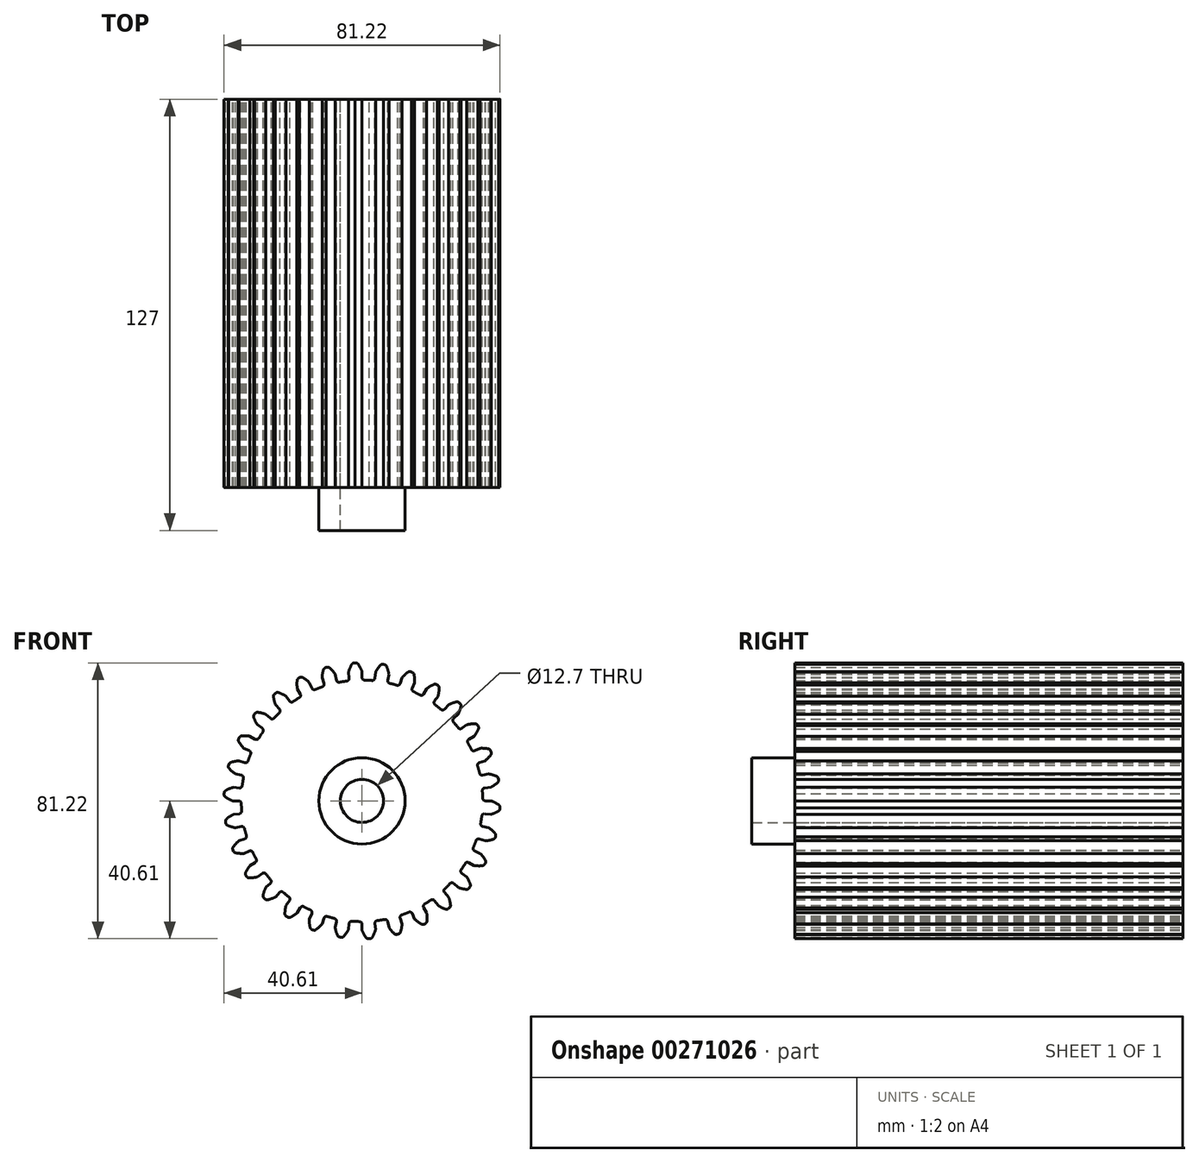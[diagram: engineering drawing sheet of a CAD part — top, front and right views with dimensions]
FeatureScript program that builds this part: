
annotation { "Feature Type Name" : "Feature", "Feature Type Description" : "" }
export const myFeature = defineFeature(function(context is Context, id is Id, definition is map)
    precondition{}
    {
        {
            var Q0;
            Q0=qCreatedBy(makeId("Front.planeOp"),FACE);
            var sketch = newSketch(context, id + "F0", { "sketchPlane" : qUnion([Q0])});
            skArc(sketch, "E0", {"start": v(-4.48, 35.28) * mm, "mid": v(1.86, -35.51) * mm, "end": v(0.77, 35.55) * mm});
            skLineSegment(sketch, "E1", {"start": v(0, 0) * mm, "end": v(-3.21, 61.32) * mm, "construction": true});
            skLineSegment(sketch, "E2", {"start": v(-1.83, 40.61) * mm, "end": v(-2.13, 40.61) * mm});
            skLineSegment(sketch, "E3", {"start": v(0, 38.1) * mm, "end": v(0, 36.34) * mm});
            skArc(sketch, "E4.trimOffspring", {"start": v(0, 38.1) * mm, "mid": v(-0.52, 39.23) * mm, "end": v(-1.2, 40.3) * mm});
            skLineSegment(sketch, "E5.MirrorCS", {"start": v(-2.43, 40.58) * mm, "end": v(-2.13, 40.61) * mm});
            skArc(sketch, "E6.MirrorCS", {"start": v(-3.98, 37.9) * mm, "mid": v(-3.58, 39.07) * mm, "end": v(-3.03, 40.2) * mm});
            skLineSegment(sketch, "E7.MirrorCS", {"start": v(-3.98, 37.9) * mm, "end": v(-3.8, 36.14) * mm});
            skPoint(sketch, "E8.orphan", {"position": v(-3.59, 34.15) * mm});
            skPoint(sketch, "E9.orphan", {"position": v(0, 34.34) * mm});
            skPoint(sketch, "E10.visualSharp", {"position": v(-2.81, 40.54) * mm});
            skArc(sketch, "E10.filletArc", {"start": v(-2.43, 40.58) * mm, "mid": v(-2.77, 40.46) * mm, "end": v(-3.03, 40.2) * mm});
            skPoint(sketch, "E11.visualSharp", {"position": v(-1.44, 40.61) * mm});
            skArc(sketch, "E11.filletArc", {"start": v(-1.2, 40.3) * mm, "mid": v(-1.47, 40.53) * mm, "end": v(-1.83, 40.61) * mm});
            skPoint(sketch, "E12.visualSharp", {"position": v(0, 35.56) * mm});
            skArc(sketch, "E12.filletArc", {"start": v(0, 36.34) * mm, "mid": v(0.22, 35.79) * mm, "end": v(0.77, 35.55) * mm});
            skPoint(sketch, "E13.visualSharp", {"position": v(-3.72, 35.37) * mm});
            skArc(sketch, "E13.filletArc", {"start": v(-4.48, 35.28) * mm, "mid": v(-3.96, 35.57) * mm, "end": v(-3.8, 36.14) * mm});
            skArc(sketch, "E14.1.0", {"start": v(-11.72, 33.57) * mm, "mid": v(-11.27, 33.97) * mm, "end": v(-11.23, 34.56) * mm});
            skLineSegment(sketch, "E14.1.1", {"start": v(-11.77, 36.24) * mm, "end": v(-11.23, 34.56) * mm});
            skArc(sketch, "E14.1.2", {"start": v(-11.77, 36.24) * mm, "mid": v(-11.63, 37.48) * mm, "end": v(-11.32, 38.69) * mm});
            skArc(sketch, "E14.1.3", {"start": v(-10.81, 39.2) * mm, "mid": v(-11.12, 39) * mm, "end": v(-11.32, 38.69) * mm});
            skLineSegment(sketch, "E14.1.4", {"start": v(-10.81, 39.2) * mm, "end": v(-10.53, 39.28) * mm});
            skLineSegment(sketch, "E14.1.5", {"start": v(-10.23, 39.35) * mm, "end": v(-10.53, 39.28) * mm});
            skArc(sketch, "E14.1.6", {"start": v(-9.54, 39.16) * mm, "mid": v(-9.87, 39.34) * mm, "end": v(-10.23, 39.35) * mm});
            skArc(sketch, "E14.1.7", {"start": v(-7.92, 37.27) * mm, "mid": v(-8.67, 38.27) * mm, "end": v(-9.54, 39.16) * mm});
            skLineSegment(sketch, "E14.1.8", {"start": v(-7.92, 37.27) * mm, "end": v(-7.56, 35.54) * mm});
            skArc(sketch, "E14.1.9", {"start": v(-7.56, 35.54) * mm, "mid": v(-7.22, 35.05) * mm, "end": v(-6.64, 34.93) * mm});
            skArc(sketch, "E14.2.0", {"start": v(-18.44, 30.4) * mm, "mid": v(-18.09, 30.88) * mm, "end": v(-18.17, 31.47) * mm});
            skLineSegment(sketch, "E14.2.1", {"start": v(-19.05, 33) * mm, "end": v(-18.17, 31.47) * mm});
            skArc(sketch, "E14.2.2", {"start": v(-19.05, 33) * mm, "mid": v(-19.16, 34.24) * mm, "end": v(-19.11, 35.49) * mm});
            skArc(sketch, "E14.2.3", {"start": v(-18.72, 36.09) * mm, "mid": v(-18.99, 35.84) * mm, "end": v(-19.11, 35.49) * mm});
            skLineSegment(sketch, "E14.2.4", {"start": v(-18.72, 36.09) * mm, "end": v(-18.46, 36.24) * mm});
            skLineSegment(sketch, "E14.2.5", {"start": v(-18.2, 36.36) * mm, "end": v(-18.46, 36.24) * mm});
            skArc(sketch, "E14.2.6", {"start": v(-17.48, 36.32) * mm, "mid": v(-17.83, 36.43) * mm, "end": v(-18.2, 36.36) * mm});
            skArc(sketch, "E14.2.7", {"start": v(-15.5, 34.8) * mm, "mid": v(-16.44, 35.63) * mm, "end": v(-17.48, 36.32) * mm});
            skLineSegment(sketch, "E14.2.8", {"start": v(-15.5, 34.8) * mm, "end": v(-14.78, 33.2) * mm});
            skArc(sketch, "E14.2.9", {"start": v(-14.78, 33.2) * mm, "mid": v(-14.35, 32.79) * mm, "end": v(-13.76, 32.8) * mm});
            skArc(sketch, "E14.3.0", {"start": v(-24.36, 25.9) * mm, "mid": v(-24.11, 26.45) * mm, "end": v(-24.32, 27) * mm});
            skLineSegment(sketch, "E14.3.1", {"start": v(-25.5, 28.31) * mm, "end": v(-24.32, 27) * mm});
            skArc(sketch, "E14.3.2", {"start": v(-25.5, 28.31) * mm, "mid": v(-25.86, 29.5) * mm, "end": v(-26.07, 30.74) * mm});
            skArc(sketch, "E14.3.3", {"start": v(-25.82, 31.4) * mm, "mid": v(-26.03, 31.1) * mm, "end": v(-26.07, 30.74) * mm});
            skLineSegment(sketch, "E14.3.4", {"start": v(-25.82, 31.4) * mm, "end": v(-25.6, 31.6) * mm});
            skLineSegment(sketch, "E14.3.5", {"start": v(-25.35, 31.78) * mm, "end": v(-25.6, 31.6) * mm});
            skArc(sketch, "E14.3.6", {"start": v(-24.65, 31.9) * mm, "mid": v(-25.01, 31.92) * mm, "end": v(-25.35, 31.78) * mm});
            skArc(sketch, "E14.3.7", {"start": v(-22.4, 30.82) * mm, "mid": v(-23.49, 31.43) * mm, "end": v(-24.65, 31.9) * mm});
            skLineSegment(sketch, "E14.3.8", {"start": v(-22.4, 30.82) * mm, "end": v(-21.36, 29.4) * mm});
            skArc(sketch, "E14.3.9", {"start": v(-21.36, 29.4) * mm, "mid": v(-20.85, 29.09) * mm, "end": v(-20.27, 29.21) * mm});
            skArc(sketch, "E14.4.0", {"start": v(-29.21, 20.27) * mm, "mid": v(-29.09, 20.85) * mm, "end": v(-29.4, 21.36) * mm});
            skLineSegment(sketch, "E14.4.1", {"start": v(-30.82, 22.4) * mm, "end": v(-29.4, 21.36) * mm});
            skArc(sketch, "E14.4.2", {"start": v(-30.82, 22.4) * mm, "mid": v(-31.43, 23.49) * mm, "end": v(-31.9, 24.65) * mm});
            skArc(sketch, "E14.4.3", {"start": v(-31.78, 25.35) * mm, "mid": v(-31.92, 25.01) * mm, "end": v(-31.9, 24.65) * mm});
            skLineSegment(sketch, "E14.4.4", {"start": v(-31.78, 25.35) * mm, "end": v(-31.6, 25.6) * mm});
            skLineSegment(sketch, "E14.4.5", {"start": v(-31.4, 25.82) * mm, "end": v(-31.6, 25.6) * mm});
            skArc(sketch, "E14.4.6", {"start": v(-30.74, 26.07) * mm, "mid": v(-31.1, 26.03) * mm, "end": v(-31.4, 25.82) * mm});
            skArc(sketch, "E14.4.7", {"start": v(-28.31, 25.5) * mm, "mid": v(-29.5, 25.86) * mm, "end": v(-30.74, 26.07) * mm});
            skLineSegment(sketch, "E14.4.8", {"start": v(-28.31, 25.5) * mm, "end": v(-27, 24.32) * mm});
            skArc(sketch, "E14.4.9", {"start": v(-27, 24.32) * mm, "mid": v(-26.45, 24.11) * mm, "end": v(-25.9, 24.36) * mm});
            skArc(sketch, "E14.5.0", {"start": v(-32.8, 13.76) * mm, "mid": v(-32.79, 14.35) * mm, "end": v(-33.2, 14.78) * mm});
            skLineSegment(sketch, "E14.5.1", {"start": v(-34.8, 15.5) * mm, "end": v(-33.2, 14.78) * mm});
            skArc(sketch, "E14.5.2", {"start": v(-34.8, 15.5) * mm, "mid": v(-35.63, 16.44) * mm, "end": v(-36.32, 17.48) * mm});
            skArc(sketch, "E14.5.3", {"start": v(-36.36, 18.2) * mm, "mid": v(-36.43, 17.83) * mm, "end": v(-36.32, 17.48) * mm});
            skLineSegment(sketch, "E14.5.4", {"start": v(-36.36, 18.2) * mm, "end": v(-36.24, 18.46) * mm});
            skLineSegment(sketch, "E14.5.5", {"start": v(-36.09, 18.72) * mm, "end": v(-36.24, 18.46) * mm});
            skArc(sketch, "E14.5.6", {"start": v(-35.49, 19.11) * mm, "mid": v(-35.84, 18.99) * mm, "end": v(-36.09, 18.72) * mm});
            skArc(sketch, "E14.5.7", {"start": v(-33, 19.05) * mm, "mid": v(-34.24, 19.16) * mm, "end": v(-35.49, 19.11) * mm});
            skLineSegment(sketch, "E14.5.8", {"start": v(-33, 19.05) * mm, "end": v(-31.47, 18.17) * mm});
            skArc(sketch, "E14.5.9", {"start": v(-31.47, 18.17) * mm, "mid": v(-30.88, 18.09) * mm, "end": v(-30.4, 18.44) * mm});
            skArc(sketch, "E14.6.0", {"start": v(-34.93, 6.64) * mm, "mid": v(-35.05, 7.22) * mm, "end": v(-35.54, 7.56) * mm});
            skLineSegment(sketch, "E14.6.1", {"start": v(-37.27, 7.92) * mm, "end": v(-35.54, 7.56) * mm});
            skArc(sketch, "E14.6.2", {"start": v(-37.27, 7.92) * mm, "mid": v(-38.27, 8.67) * mm, "end": v(-39.16, 9.54) * mm});
            skArc(sketch, "E14.6.3", {"start": v(-39.35, 10.23) * mm, "mid": v(-39.34, 9.87) * mm, "end": v(-39.16, 9.54) * mm});
            skLineSegment(sketch, "E14.6.4", {"start": v(-39.35, 10.23) * mm, "end": v(-39.28, 10.53) * mm});
            skLineSegment(sketch, "E14.6.5", {"start": v(-39.2, 10.81) * mm, "end": v(-39.28, 10.53) * mm});
            skArc(sketch, "E14.6.6", {"start": v(-38.69, 11.32) * mm, "mid": v(-39, 11.12) * mm, "end": v(-39.2, 10.81) * mm});
            skArc(sketch, "E14.6.7", {"start": v(-36.24, 11.77) * mm, "mid": v(-37.48, 11.63) * mm, "end": v(-38.69, 11.32) * mm});
            skLineSegment(sketch, "E14.6.8", {"start": v(-36.24, 11.77) * mm, "end": v(-34.56, 11.23) * mm});
            skArc(sketch, "E14.6.9", {"start": v(-34.56, 11.23) * mm, "mid": v(-33.97, 11.27) * mm, "end": v(-33.57, 11.72) * mm});
            skArc(sketch, "E14.7.0", {"start": v(-35.55, -0.77) * mm, "mid": v(-35.79, -0.22) * mm, "end": v(-36.34, 0) * mm});
            skLineSegment(sketch, "E14.7.1", {"start": v(-38.1, 0) * mm, "end": v(-36.34, 0) * mm});
            skArc(sketch, "E14.7.2", {"start": v(-38.1, 0) * mm, "mid": v(-39.23, 0.52) * mm, "end": v(-40.3, 1.2) * mm});
            skArc(sketch, "E14.7.3", {"start": v(-40.61, 1.83) * mm, "mid": v(-40.53, 1.47) * mm, "end": v(-40.3, 1.2) * mm});
            skLineSegment(sketch, "E14.7.4", {"start": v(-40.61, 1.83) * mm, "end": v(-40.61, 2.13) * mm});
            skLineSegment(sketch, "E14.7.5", {"start": v(-40.58, 2.43) * mm, "end": v(-40.61, 2.13) * mm});
            skArc(sketch, "E14.7.6", {"start": v(-40.2, 3.03) * mm, "mid": v(-40.46, 2.77) * mm, "end": v(-40.58, 2.43) * mm});
            skArc(sketch, "E14.7.7", {"start": v(-37.9, 3.98) * mm, "mid": v(-39.07, 3.58) * mm, "end": v(-40.2, 3.03) * mm});
            skLineSegment(sketch, "E14.7.8", {"start": v(-37.9, 3.98) * mm, "end": v(-36.14, 3.8) * mm});
            skArc(sketch, "E14.7.9", {"start": v(-36.14, 3.8) * mm, "mid": v(-35.57, 3.96) * mm, "end": v(-35.28, 4.48) * mm});
            skArc(sketch, "E14.8.0", {"start": v(-34.61, -8.15) * mm, "mid": v(-34.96, -7.66) * mm, "end": v(-35.54, -7.56) * mm});
            skLineSegment(sketch, "E14.8.1", {"start": v(-37.27, -7.92) * mm, "end": v(-35.54, -7.56) * mm});
            skArc(sketch, "E14.8.2", {"start": v(-37.27, -7.92) * mm, "mid": v(-38.49, -7.64) * mm, "end": v(-39.66, -7.21) * mm});
            skArc(sketch, "E14.8.3", {"start": v(-40.1, -6.66) * mm, "mid": v(-39.95, -6.99) * mm, "end": v(-39.66, -7.21) * mm});
            skLineSegment(sketch, "E14.8.4", {"start": v(-40.1, -6.66) * mm, "end": v(-40.17, -6.36) * mm});
            skLineSegment(sketch, "E14.8.5", {"start": v(-40.2, -6.06) * mm, "end": v(-40.17, -6.36) * mm});
            skArc(sketch, "E14.8.6", {"start": v(-39.95, -5.4) * mm, "mid": v(-40.15, -5.7) * mm, "end": v(-40.2, -6.06) * mm});
            skArc(sketch, "E14.8.7", {"start": v(-37.9, -3.98) * mm, "mid": v(-38.96, -4.62) * mm, "end": v(-39.95, -5.4) * mm});
            skLineSegment(sketch, "E14.8.8", {"start": v(-37.9, -3.98) * mm, "end": v(-36.14, -3.8) * mm});
            skArc(sketch, "E14.8.9", {"start": v(-36.14, -3.8) * mm, "mid": v(-35.62, -3.52) * mm, "end": v(-35.44, -2.95) * mm});
            skArc(sketch, "E14.9.0", {"start": v(-32.16, -15.16) * mm, "mid": v(-32.6, -14.76) * mm, "end": v(-33.2, -14.78) * mm});
            skLineSegment(sketch, "E14.9.1", {"start": v(-34.8, -15.5) * mm, "end": v(-33.2, -14.78) * mm});
            skArc(sketch, "E14.9.2", {"start": v(-34.8, -15.5) * mm, "mid": v(-36.06, -15.48) * mm, "end": v(-37.3, -15.3) * mm});
            skArc(sketch, "E14.9.3", {"start": v(-37.85, -14.85) * mm, "mid": v(-37.62, -15.14) * mm, "end": v(-37.3, -15.3) * mm});
            skLineSegment(sketch, "E14.9.4", {"start": v(-37.85, -14.85) * mm, "end": v(-37.97, -14.57) * mm});
            skLineSegment(sketch, "E14.9.5", {"start": v(-38.06, -14.29) * mm, "end": v(-37.97, -14.57) * mm});
            skArc(sketch, "E14.9.6", {"start": v(-37.95, -13.58) * mm, "mid": v(-38.1, -13.92) * mm, "end": v(-38.06, -14.29) * mm});
            skArc(sketch, "E14.9.7", {"start": v(-36.24, -11.77) * mm, "mid": v(-37.15, -12.62) * mm, "end": v(-37.95, -13.58) * mm});
            skLineSegment(sketch, "E14.9.8", {"start": v(-36.24, -11.77) * mm, "end": v(-34.56, -11.23) * mm});
            skArc(sketch, "E14.9.9", {"start": v(-34.56, -11.23) * mm, "mid": v(-34.1, -10.85) * mm, "end": v(-34.05, -10.25) * mm});
            skArc(sketch, "E14.10.0", {"start": v(-28.3, -21.52) * mm, "mid": v(-28.82, -21.22) * mm, "end": v(-29.4, -21.36) * mm});
            skLineSegment(sketch, "E14.10.1", {"start": v(-30.82, -22.4) * mm, "end": v(-29.4, -21.36) * mm});
            skArc(sketch, "E14.10.2", {"start": v(-30.82, -22.4) * mm, "mid": v(-32.05, -22.64) * mm, "end": v(-33.3, -22.72) * mm});
            skArc(sketch, "E14.10.3", {"start": v(-33.93, -22.4) * mm, "mid": v(-33.65, -22.63) * mm, "end": v(-33.3, -22.72) * mm});
            skLineSegment(sketch, "E14.10.4", {"start": v(-33.93, -22.4) * mm, "end": v(-34.1, -22.15) * mm});
            skLineSegment(sketch, "E14.10.5", {"start": v(-34.26, -21.9) * mm, "end": v(-34.1, -22.15) * mm});
            skArc(sketch, "E14.10.6", {"start": v(-34.3, -21.18) * mm, "mid": v(-34.36, -21.54) * mm, "end": v(-34.26, -21.9) * mm});
            skArc(sketch, "E14.10.7", {"start": v(-33, -19.05) * mm, "mid": v(-33.72, -20.07) * mm, "end": v(-34.3, -21.18) * mm});
            skLineSegment(sketch, "E14.10.8", {"start": v(-33, -19.05) * mm, "end": v(-31.47, -18.17) * mm});
            skArc(sketch, "E14.10.9", {"start": v(-31.47, -18.17) * mm, "mid": v(-31.1, -17.7) * mm, "end": v(-31.17, -17.1) * mm});
            skArc(sketch, "E14.11.0", {"start": v(-23.22, -26.94) * mm, "mid": v(-23.78, -26.75) * mm, "end": v(-24.32, -27) * mm});
            skLineSegment(sketch, "E14.11.1", {"start": v(-25.5, -28.31) * mm, "end": v(-24.32, -27) * mm});
            skArc(sketch, "E14.11.2", {"start": v(-25.5, -28.31) * mm, "mid": v(-26.64, -28.8) * mm, "end": v(-27.85, -29.14) * mm});
            skArc(sketch, "E14.11.3", {"start": v(-28.54, -28.96) * mm, "mid": v(-28.21, -29.13) * mm, "end": v(-27.85, -29.14) * mm});
            skLineSegment(sketch, "E14.11.4", {"start": v(-28.54, -28.96) * mm, "end": v(-28.76, -28.76) * mm});
            skLineSegment(sketch, "E14.11.5", {"start": v(-28.96, -28.54) * mm, "end": v(-28.76, -28.76) * mm});
            skArc(sketch, "E14.11.6", {"start": v(-29.14, -27.85) * mm, "mid": v(-29.13, -28.21) * mm, "end": v(-28.96, -28.54) * mm});
            skArc(sketch, "E14.11.7", {"start": v(-28.31, -25.5) * mm, "mid": v(-28.8, -26.64) * mm, "end": v(-29.14, -27.85) * mm});
            skLineSegment(sketch, "E14.11.8", {"start": v(-28.31, -25.5) * mm, "end": v(-27, -24.32) * mm});
            skArc(sketch, "E14.11.9", {"start": v(-27, -24.32) * mm, "mid": v(-26.75, -23.78) * mm, "end": v(-26.94, -23.22) * mm});
            skArc(sketch, "E14.12.0", {"start": v(-17.1, -31.17) * mm, "mid": v(-17.7, -31.1) * mm, "end": v(-18.17, -31.47) * mm});
            skLineSegment(sketch, "E14.12.1", {"start": v(-19.05, -33) * mm, "end": v(-18.17, -31.47) * mm});
            skArc(sketch, "E14.12.2", {"start": v(-19.05, -33) * mm, "mid": v(-20.07, -33.72) * mm, "end": v(-21.18, -34.3) * mm});
            skArc(sketch, "E14.12.3", {"start": v(-21.9, -34.26) * mm, "mid": v(-21.54, -34.36) * mm, "end": v(-21.18, -34.3) * mm});
            skLineSegment(sketch, "E14.12.4", {"start": v(-21.9, -34.26) * mm, "end": v(-22.15, -34.1) * mm});
            skLineSegment(sketch, "E14.12.5", {"start": v(-22.4, -33.93) * mm, "end": v(-22.15, -34.1) * mm});
            skArc(sketch, "E14.12.6", {"start": v(-22.72, -33.3) * mm, "mid": v(-22.63, -33.65) * mm, "end": v(-22.4, -33.93) * mm});
            skArc(sketch, "E14.12.7", {"start": v(-22.4, -30.82) * mm, "mid": v(-22.64, -32.05) * mm, "end": v(-22.72, -33.3) * mm});
            skLineSegment(sketch, "E14.12.8", {"start": v(-22.4, -30.82) * mm, "end": v(-21.36, -29.4) * mm});
            skArc(sketch, "E14.12.9", {"start": v(-21.36, -29.4) * mm, "mid": v(-21.22, -28.82) * mm, "end": v(-21.52, -28.3) * mm});
            skArc(sketch, "E14.13.0", {"start": v(-10.25, -34.05) * mm, "mid": v(-10.85, -34.1) * mm, "end": v(-11.23, -34.56) * mm});
            skLineSegment(sketch, "E14.13.1", {"start": v(-11.77, -36.24) * mm, "end": v(-11.23, -34.56) * mm});
            skArc(sketch, "E14.13.2", {"start": v(-11.77, -36.24) * mm, "mid": v(-12.62, -37.15) * mm, "end": v(-13.58, -37.95) * mm});
            skArc(sketch, "E14.13.3", {"start": v(-14.29, -38.06) * mm, "mid": v(-13.92, -38.1) * mm, "end": v(-13.58, -37.95) * mm});
            skLineSegment(sketch, "E14.13.4", {"start": v(-14.29, -38.06) * mm, "end": v(-14.57, -37.97) * mm});
            skLineSegment(sketch, "E14.13.5", {"start": v(-14.85, -37.85) * mm, "end": v(-14.57, -37.97) * mm});
            skArc(sketch, "E14.13.6", {"start": v(-15.3, -37.3) * mm, "mid": v(-15.14, -37.62) * mm, "end": v(-14.85, -37.85) * mm});
            skArc(sketch, "E14.13.7", {"start": v(-15.5, -34.8) * mm, "mid": v(-15.48, -36.06) * mm, "end": v(-15.3, -37.3) * mm});
            skLineSegment(sketch, "E14.13.8", {"start": v(-15.5, -34.8) * mm, "end": v(-14.78, -33.2) * mm});
            skArc(sketch, "E14.13.9", {"start": v(-14.78, -33.2) * mm, "mid": v(-14.76, -32.6) * mm, "end": v(-15.16, -32.16) * mm});
            skArc(sketch, "E14.14.0", {"start": v(-2.95, -35.44) * mm, "mid": v(-3.52, -35.62) * mm, "end": v(-3.8, -36.14) * mm});
            skLineSegment(sketch, "E14.14.1", {"start": v(-3.98, -37.9) * mm, "end": v(-3.8, -36.14) * mm});
            skArc(sketch, "E14.14.2", {"start": v(-3.98, -37.9) * mm, "mid": v(-4.62, -38.96) * mm, "end": v(-5.4, -39.95) * mm});
            skArc(sketch, "E14.14.3", {"start": v(-6.06, -40.2) * mm, "mid": v(-5.7, -40.15) * mm, "end": v(-5.4, -39.95) * mm});
            skLineSegment(sketch, "E14.14.4", {"start": v(-6.06, -40.2) * mm, "end": v(-6.36, -40.17) * mm});
            skLineSegment(sketch, "E14.14.5", {"start": v(-6.66, -40.1) * mm, "end": v(-6.36, -40.17) * mm});
            skArc(sketch, "E14.14.6", {"start": v(-7.21, -39.66) * mm, "mid": v(-6.99, -39.95) * mm, "end": v(-6.66, -40.1) * mm});
            skArc(sketch, "E14.14.7", {"start": v(-7.92, -37.27) * mm, "mid": v(-7.64, -38.49) * mm, "end": v(-7.21, -39.66) * mm});
            skLineSegment(sketch, "E14.14.8", {"start": v(-7.92, -37.27) * mm, "end": v(-7.56, -35.54) * mm});
            skArc(sketch, "E14.14.9", {"start": v(-7.56, -35.54) * mm, "mid": v(-7.66, -34.96) * mm, "end": v(-8.15, -34.61) * mm});
            skArc(sketch, "E14.15.0", {"start": v(4.48, -35.28) * mm, "mid": v(3.96, -35.57) * mm, "end": v(3.8, -36.14) * mm});
            skLineSegment(sketch, "E14.15.1", {"start": v(3.98, -37.9) * mm, "end": v(3.8, -36.14) * mm});
            skArc(sketch, "E14.15.2", {"start": v(3.98, -37.9) * mm, "mid": v(3.58, -39.07) * mm, "end": v(3.03, -40.2) * mm});
            skArc(sketch, "E14.15.3", {"start": v(2.43, -40.58) * mm, "mid": v(2.77, -40.46) * mm, "end": v(3.03, -40.2) * mm});
            skLineSegment(sketch, "E14.15.4", {"start": v(2.43, -40.58) * mm, "end": v(2.13, -40.61) * mm});
            skLineSegment(sketch, "E14.15.5", {"start": v(1.83, -40.61) * mm, "end": v(2.13, -40.61) * mm});
            skArc(sketch, "E14.15.6", {"start": v(1.2, -40.3) * mm, "mid": v(1.47, -40.53) * mm, "end": v(1.83, -40.61) * mm});
            skArc(sketch, "E14.15.7", {"start": v(0, -38.1) * mm, "mid": v(0.52, -39.23) * mm, "end": v(1.2, -40.3) * mm});
            skLineSegment(sketch, "E14.15.8", {"start": v(0, -38.1) * mm, "end": v(0, -36.34) * mm});
            skArc(sketch, "E14.15.9", {"start": v(0, -36.34) * mm, "mid": v(-0.22, -35.79) * mm, "end": v(-0.77, -35.55) * mm});
            skArc(sketch, "E14.16.0", {"start": v(11.72, -33.57) * mm, "mid": v(11.27, -33.97) * mm, "end": v(11.23, -34.56) * mm});
            skLineSegment(sketch, "E14.16.1", {"start": v(11.77, -36.24) * mm, "end": v(11.23, -34.56) * mm});
            skArc(sketch, "E14.16.2", {"start": v(11.77, -36.24) * mm, "mid": v(11.63, -37.48) * mm, "end": v(11.32, -38.69) * mm});
            skArc(sketch, "E14.16.3", {"start": v(10.81, -39.2) * mm, "mid": v(11.12, -39) * mm, "end": v(11.32, -38.69) * mm});
            skLineSegment(sketch, "E14.16.4", {"start": v(10.81, -39.2) * mm, "end": v(10.53, -39.28) * mm});
            skLineSegment(sketch, "E14.16.5", {"start": v(10.23, -39.35) * mm, "end": v(10.53, -39.28) * mm});
            skArc(sketch, "E14.16.6", {"start": v(9.54, -39.16) * mm, "mid": v(9.87, -39.34) * mm, "end": v(10.23, -39.35) * mm});
            skArc(sketch, "E14.16.7", {"start": v(7.92, -37.27) * mm, "mid": v(8.67, -38.27) * mm, "end": v(9.54, -39.16) * mm});
            skLineSegment(sketch, "E14.16.8", {"start": v(7.92, -37.27) * mm, "end": v(7.56, -35.54) * mm});
            skArc(sketch, "E14.16.9", {"start": v(7.56, -35.54) * mm, "mid": v(7.22, -35.05) * mm, "end": v(6.64, -34.93) * mm});
            skArc(sketch, "E14.17.0", {"start": v(18.44, -30.4) * mm, "mid": v(18.09, -30.88) * mm, "end": v(18.17, -31.47) * mm});
            skLineSegment(sketch, "E14.17.1", {"start": v(19.05, -33) * mm, "end": v(18.17, -31.47) * mm});
            skArc(sketch, "E14.17.2", {"start": v(19.05, -33) * mm, "mid": v(19.16, -34.24) * mm, "end": v(19.11, -35.49) * mm});
            skArc(sketch, "E14.17.3", {"start": v(18.72, -36.09) * mm, "mid": v(18.99, -35.84) * mm, "end": v(19.11, -35.49) * mm});
            skLineSegment(sketch, "E14.17.4", {"start": v(18.72, -36.09) * mm, "end": v(18.46, -36.24) * mm});
            skLineSegment(sketch, "E14.17.5", {"start": v(18.2, -36.36) * mm, "end": v(18.46, -36.24) * mm});
            skArc(sketch, "E14.17.6", {"start": v(17.48, -36.32) * mm, "mid": v(17.83, -36.43) * mm, "end": v(18.2, -36.36) * mm});
            skArc(sketch, "E14.17.7", {"start": v(15.5, -34.8) * mm, "mid": v(16.44, -35.63) * mm, "end": v(17.48, -36.32) * mm});
            skLineSegment(sketch, "E14.17.8", {"start": v(15.5, -34.8) * mm, "end": v(14.78, -33.2) * mm});
            skArc(sketch, "E14.17.9", {"start": v(14.78, -33.2) * mm, "mid": v(14.35, -32.79) * mm, "end": v(13.76, -32.8) * mm});
            skArc(sketch, "E14.18.0", {"start": v(24.36, -25.9) * mm, "mid": v(24.11, -26.45) * mm, "end": v(24.32, -27) * mm});
            skLineSegment(sketch, "E14.18.1", {"start": v(25.5, -28.31) * mm, "end": v(24.32, -27) * mm});
            skArc(sketch, "E14.18.2", {"start": v(25.5, -28.31) * mm, "mid": v(25.86, -29.5) * mm, "end": v(26.07, -30.74) * mm});
            skArc(sketch, "E14.18.3", {"start": v(25.82, -31.4) * mm, "mid": v(26.03, -31.1) * mm, "end": v(26.07, -30.74) * mm});
            skLineSegment(sketch, "E14.18.4", {"start": v(25.82, -31.4) * mm, "end": v(25.6, -31.6) * mm});
            skLineSegment(sketch, "E14.18.5", {"start": v(25.35, -31.78) * mm, "end": v(25.6, -31.6) * mm});
            skArc(sketch, "E14.18.6", {"start": v(24.65, -31.9) * mm, "mid": v(25.01, -31.92) * mm, "end": v(25.35, -31.78) * mm});
            skArc(sketch, "E14.18.7", {"start": v(22.4, -30.82) * mm, "mid": v(23.49, -31.43) * mm, "end": v(24.65, -31.9) * mm});
            skLineSegment(sketch, "E14.18.8", {"start": v(22.4, -30.82) * mm, "end": v(21.36, -29.4) * mm});
            skArc(sketch, "E14.18.9", {"start": v(21.36, -29.4) * mm, "mid": v(20.85, -29.09) * mm, "end": v(20.27, -29.21) * mm});
            skArc(sketch, "E14.19.0", {"start": v(29.21, -20.27) * mm, "mid": v(29.09, -20.85) * mm, "end": v(29.4, -21.36) * mm});
            skLineSegment(sketch, "E14.19.1", {"start": v(30.82, -22.4) * mm, "end": v(29.4, -21.36) * mm});
            skArc(sketch, "E14.19.2", {"start": v(30.82, -22.4) * mm, "mid": v(31.43, -23.49) * mm, "end": v(31.9, -24.65) * mm});
            skArc(sketch, "E14.19.3", {"start": v(31.78, -25.35) * mm, "mid": v(31.92, -25.01) * mm, "end": v(31.9, -24.65) * mm});
            skLineSegment(sketch, "E14.19.4", {"start": v(31.78, -25.35) * mm, "end": v(31.6, -25.6) * mm});
            skLineSegment(sketch, "E14.19.5", {"start": v(31.4, -25.82) * mm, "end": v(31.6, -25.6) * mm});
            skArc(sketch, "E14.19.6", {"start": v(30.74, -26.07) * mm, "mid": v(31.1, -26.03) * mm, "end": v(31.4, -25.82) * mm});
            skArc(sketch, "E14.19.7", {"start": v(28.31, -25.5) * mm, "mid": v(29.5, -25.86) * mm, "end": v(30.74, -26.07) * mm});
            skLineSegment(sketch, "E14.19.8", {"start": v(28.31, -25.5) * mm, "end": v(27, -24.32) * mm});
            skArc(sketch, "E14.19.9", {"start": v(27, -24.32) * mm, "mid": v(26.45, -24.11) * mm, "end": v(25.9, -24.36) * mm});
            skArc(sketch, "E14.20.0", {"start": v(32.8, -13.76) * mm, "mid": v(32.79, -14.35) * mm, "end": v(33.2, -14.78) * mm});
            skLineSegment(sketch, "E14.20.1", {"start": v(34.8, -15.5) * mm, "end": v(33.2, -14.78) * mm});
            skArc(sketch, "E14.20.2", {"start": v(34.8, -15.5) * mm, "mid": v(35.63, -16.44) * mm, "end": v(36.32, -17.48) * mm});
            skArc(sketch, "E14.20.3", {"start": v(36.36, -18.2) * mm, "mid": v(36.43, -17.83) * mm, "end": v(36.32, -17.48) * mm});
            skLineSegment(sketch, "E14.20.4", {"start": v(36.36, -18.2) * mm, "end": v(36.24, -18.46) * mm});
            skLineSegment(sketch, "E14.20.5", {"start": v(36.09, -18.72) * mm, "end": v(36.24, -18.46) * mm});
            skArc(sketch, "E14.20.6", {"start": v(35.49, -19.11) * mm, "mid": v(35.84, -18.99) * mm, "end": v(36.09, -18.72) * mm});
            skArc(sketch, "E14.20.7", {"start": v(33, -19.05) * mm, "mid": v(34.24, -19.16) * mm, "end": v(35.49, -19.11) * mm});
            skLineSegment(sketch, "E14.20.8", {"start": v(33, -19.05) * mm, "end": v(31.47, -18.17) * mm});
            skArc(sketch, "E14.20.9", {"start": v(31.47, -18.17) * mm, "mid": v(30.88, -18.09) * mm, "end": v(30.4, -18.44) * mm});
            skArc(sketch, "E14.21.0", {"start": v(34.93, -6.64) * mm, "mid": v(35.05, -7.22) * mm, "end": v(35.54, -7.56) * mm});
            skLineSegment(sketch, "E14.21.1", {"start": v(37.27, -7.92) * mm, "end": v(35.54, -7.56) * mm});
            skArc(sketch, "E14.21.2", {"start": v(37.27, -7.92) * mm, "mid": v(38.27, -8.67) * mm, "end": v(39.16, -9.54) * mm});
            skArc(sketch, "E14.21.3", {"start": v(39.35, -10.23) * mm, "mid": v(39.34, -9.87) * mm, "end": v(39.16, -9.54) * mm});
            skLineSegment(sketch, "E14.21.4", {"start": v(39.35, -10.23) * mm, "end": v(39.28, -10.53) * mm});
            skLineSegment(sketch, "E14.21.5", {"start": v(39.2, -10.81) * mm, "end": v(39.28, -10.53) * mm});
            skArc(sketch, "E14.21.6", {"start": v(38.69, -11.32) * mm, "mid": v(39, -11.12) * mm, "end": v(39.2, -10.81) * mm});
            skArc(sketch, "E14.21.7", {"start": v(36.24, -11.77) * mm, "mid": v(37.48, -11.63) * mm, "end": v(38.69, -11.32) * mm});
            skLineSegment(sketch, "E14.21.8", {"start": v(36.24, -11.77) * mm, "end": v(34.56, -11.23) * mm});
            skArc(sketch, "E14.21.9", {"start": v(34.56, -11.23) * mm, "mid": v(33.97, -11.27) * mm, "end": v(33.57, -11.72) * mm});
            skArc(sketch, "E14.22.0", {"start": v(35.55, 0.77) * mm, "mid": v(35.79, 0.22) * mm, "end": v(36.34, 0) * mm});
            skLineSegment(sketch, "E14.22.1", {"start": v(38.1, 0) * mm, "end": v(36.34, 0) * mm});
            skArc(sketch, "E14.22.2", {"start": v(38.1, 0) * mm, "mid": v(39.23, -0.52) * mm, "end": v(40.3, -1.2) * mm});
            skArc(sketch, "E14.22.3", {"start": v(40.61, -1.83) * mm, "mid": v(40.53, -1.47) * mm, "end": v(40.3, -1.2) * mm});
            skLineSegment(sketch, "E14.22.4", {"start": v(40.61, -1.83) * mm, "end": v(40.61, -2.13) * mm});
            skLineSegment(sketch, "E14.22.5", {"start": v(40.58, -2.43) * mm, "end": v(40.61, -2.13) * mm});
            skArc(sketch, "E14.22.6", {"start": v(40.2, -3.03) * mm, "mid": v(40.46, -2.77) * mm, "end": v(40.58, -2.43) * mm});
            skArc(sketch, "E14.22.7", {"start": v(37.9, -3.98) * mm, "mid": v(39.07, -3.58) * mm, "end": v(40.2, -3.03) * mm});
            skLineSegment(sketch, "E14.22.8", {"start": v(37.9, -3.98) * mm, "end": v(36.14, -3.8) * mm});
            skArc(sketch, "E14.22.9", {"start": v(36.14, -3.8) * mm, "mid": v(35.57, -3.96) * mm, "end": v(35.28, -4.48) * mm});
            skArc(sketch, "E14.23.0", {"start": v(34.61, 8.15) * mm, "mid": v(34.96, 7.66) * mm, "end": v(35.54, 7.56) * mm});
            skLineSegment(sketch, "E14.23.1", {"start": v(37.27, 7.92) * mm, "end": v(35.54, 7.56) * mm});
            skArc(sketch, "E14.23.2", {"start": v(37.27, 7.92) * mm, "mid": v(38.49, 7.64) * mm, "end": v(39.66, 7.21) * mm});
            skArc(sketch, "E14.23.3", {"start": v(40.1, 6.66) * mm, "mid": v(39.95, 6.99) * mm, "end": v(39.66, 7.21) * mm});
            skLineSegment(sketch, "E14.23.4", {"start": v(40.1, 6.66) * mm, "end": v(40.17, 6.36) * mm});
            skLineSegment(sketch, "E14.23.5", {"start": v(40.2, 6.06) * mm, "end": v(40.17, 6.36) * mm});
            skArc(sketch, "E14.23.6", {"start": v(39.95, 5.4) * mm, "mid": v(40.15, 5.7) * mm, "end": v(40.2, 6.06) * mm});
            skArc(sketch, "E14.23.7", {"start": v(37.9, 3.98) * mm, "mid": v(38.96, 4.62) * mm, "end": v(39.95, 5.4) * mm});
            skLineSegment(sketch, "E14.23.8", {"start": v(37.9, 3.98) * mm, "end": v(36.14, 3.8) * mm});
            skArc(sketch, "E14.23.9", {"start": v(36.14, 3.8) * mm, "mid": v(35.62, 3.52) * mm, "end": v(35.44, 2.95) * mm});
            skArc(sketch, "E14.24.0", {"start": v(32.16, 15.16) * mm, "mid": v(32.6, 14.76) * mm, "end": v(33.2, 14.78) * mm});
            skLineSegment(sketch, "E14.24.1", {"start": v(34.8, 15.5) * mm, "end": v(33.2, 14.78) * mm});
            skArc(sketch, "E14.24.2", {"start": v(34.8, 15.5) * mm, "mid": v(36.06, 15.48) * mm, "end": v(37.3, 15.3) * mm});
            skArc(sketch, "E14.24.3", {"start": v(37.85, 14.85) * mm, "mid": v(37.62, 15.14) * mm, "end": v(37.3, 15.3) * mm});
            skLineSegment(sketch, "E14.24.4", {"start": v(37.85, 14.85) * mm, "end": v(37.97, 14.57) * mm});
            skLineSegment(sketch, "E14.24.5", {"start": v(38.06, 14.29) * mm, "end": v(37.97, 14.57) * mm});
            skArc(sketch, "E14.24.6", {"start": v(37.95, 13.58) * mm, "mid": v(38.1, 13.92) * mm, "end": v(38.06, 14.29) * mm});
            skArc(sketch, "E14.24.7", {"start": v(36.24, 11.77) * mm, "mid": v(37.15, 12.62) * mm, "end": v(37.95, 13.58) * mm});
            skLineSegment(sketch, "E14.24.8", {"start": v(36.24, 11.77) * mm, "end": v(34.56, 11.23) * mm});
            skArc(sketch, "E14.24.9", {"start": v(34.56, 11.23) * mm, "mid": v(34.1, 10.85) * mm, "end": v(34.05, 10.25) * mm});
            skArc(sketch, "E14.25.0", {"start": v(28.3, 21.52) * mm, "mid": v(28.82, 21.22) * mm, "end": v(29.4, 21.36) * mm});
            skLineSegment(sketch, "E14.25.1", {"start": v(30.82, 22.4) * mm, "end": v(29.4, 21.36) * mm});
            skArc(sketch, "E14.25.2", {"start": v(30.82, 22.4) * mm, "mid": v(32.05, 22.64) * mm, "end": v(33.3, 22.72) * mm});
            skArc(sketch, "E14.25.3", {"start": v(33.93, 22.4) * mm, "mid": v(33.65, 22.63) * mm, "end": v(33.3, 22.72) * mm});
            skLineSegment(sketch, "E14.25.4", {"start": v(33.93, 22.4) * mm, "end": v(34.1, 22.15) * mm});
            skLineSegment(sketch, "E14.25.5", {"start": v(34.26, 21.9) * mm, "end": v(34.1, 22.15) * mm});
            skArc(sketch, "E14.25.6", {"start": v(34.3, 21.18) * mm, "mid": v(34.36, 21.54) * mm, "end": v(34.26, 21.9) * mm});
            skArc(sketch, "E14.25.7", {"start": v(33, 19.05) * mm, "mid": v(33.72, 20.07) * mm, "end": v(34.3, 21.18) * mm});
            skLineSegment(sketch, "E14.25.8", {"start": v(33, 19.05) * mm, "end": v(31.47, 18.17) * mm});
            skArc(sketch, "E14.25.9", {"start": v(31.47, 18.17) * mm, "mid": v(31.1, 17.7) * mm, "end": v(31.17, 17.1) * mm});
            skArc(sketch, "E14.26.0", {"start": v(23.22, 26.94) * mm, "mid": v(23.78, 26.75) * mm, "end": v(24.32, 27) * mm});
            skLineSegment(sketch, "E14.26.1", {"start": v(25.5, 28.31) * mm, "end": v(24.32, 27) * mm});
            skArc(sketch, "E14.26.2", {"start": v(25.5, 28.31) * mm, "mid": v(26.64, 28.8) * mm, "end": v(27.85, 29.14) * mm});
            skArc(sketch, "E14.26.3", {"start": v(28.54, 28.96) * mm, "mid": v(28.21, 29.13) * mm, "end": v(27.85, 29.14) * mm});
            skLineSegment(sketch, "E14.26.4", {"start": v(28.54, 28.96) * mm, "end": v(28.76, 28.76) * mm});
            skLineSegment(sketch, "E14.26.5", {"start": v(28.96, 28.54) * mm, "end": v(28.76, 28.76) * mm});
            skArc(sketch, "E14.26.6", {"start": v(29.14, 27.85) * mm, "mid": v(29.13, 28.21) * mm, "end": v(28.96, 28.54) * mm});
            skArc(sketch, "E14.26.7", {"start": v(28.31, 25.5) * mm, "mid": v(28.8, 26.64) * mm, "end": v(29.14, 27.85) * mm});
            skLineSegment(sketch, "E14.26.8", {"start": v(28.31, 25.5) * mm, "end": v(27, 24.32) * mm});
            skArc(sketch, "E14.26.9", {"start": v(27, 24.32) * mm, "mid": v(26.75, 23.78) * mm, "end": v(26.94, 23.22) * mm});
            skArc(sketch, "E14.27.0", {"start": v(17.1, 31.17) * mm, "mid": v(17.7, 31.1) * mm, "end": v(18.17, 31.47) * mm});
            skLineSegment(sketch, "E14.27.1", {"start": v(19.05, 33) * mm, "end": v(18.17, 31.47) * mm});
            skArc(sketch, "E14.27.2", {"start": v(19.05, 33) * mm, "mid": v(20.07, 33.72) * mm, "end": v(21.18, 34.3) * mm});
            skArc(sketch, "E14.27.3", {"start": v(21.9, 34.26) * mm, "mid": v(21.54, 34.36) * mm, "end": v(21.18, 34.3) * mm});
            skLineSegment(sketch, "E14.27.4", {"start": v(21.9, 34.26) * mm, "end": v(22.15, 34.1) * mm});
            skLineSegment(sketch, "E14.27.5", {"start": v(22.4, 33.93) * mm, "end": v(22.15, 34.1) * mm});
            skArc(sketch, "E14.27.6", {"start": v(22.72, 33.3) * mm, "mid": v(22.63, 33.65) * mm, "end": v(22.4, 33.93) * mm});
            skArc(sketch, "E14.27.7", {"start": v(22.4, 30.82) * mm, "mid": v(22.64, 32.05) * mm, "end": v(22.72, 33.3) * mm});
            skLineSegment(sketch, "E14.27.8", {"start": v(22.4, 30.82) * mm, "end": v(21.36, 29.4) * mm});
            skArc(sketch, "E14.27.9", {"start": v(21.36, 29.4) * mm, "mid": v(21.22, 28.82) * mm, "end": v(21.52, 28.3) * mm});
            skArc(sketch, "E14.28.0", {"start": v(10.25, 34.05) * mm, "mid": v(10.85, 34.1) * mm, "end": v(11.23, 34.56) * mm});
            skLineSegment(sketch, "E14.28.1", {"start": v(11.77, 36.24) * mm, "end": v(11.23, 34.56) * mm});
            skArc(sketch, "E14.28.2", {"start": v(11.77, 36.24) * mm, "mid": v(12.62, 37.15) * mm, "end": v(13.58, 37.95) * mm});
            skArc(sketch, "E14.28.3", {"start": v(14.29, 38.06) * mm, "mid": v(13.92, 38.1) * mm, "end": v(13.58, 37.95) * mm});
            skLineSegment(sketch, "E14.28.4", {"start": v(14.29, 38.06) * mm, "end": v(14.57, 37.97) * mm});
            skLineSegment(sketch, "E14.28.5", {"start": v(14.85, 37.85) * mm, "end": v(14.57, 37.97) * mm});
            skArc(sketch, "E14.28.6", {"start": v(15.3, 37.3) * mm, "mid": v(15.14, 37.62) * mm, "end": v(14.85, 37.85) * mm});
            skArc(sketch, "E14.28.7", {"start": v(15.5, 34.8) * mm, "mid": v(15.48, 36.06) * mm, "end": v(15.3, 37.3) * mm});
            skLineSegment(sketch, "E14.28.8", {"start": v(15.5, 34.8) * mm, "end": v(14.78, 33.2) * mm});
            skArc(sketch, "E14.28.9", {"start": v(14.78, 33.2) * mm, "mid": v(14.76, 32.6) * mm, "end": v(15.16, 32.16) * mm});
            skArc(sketch, "E14.29.0", {"start": v(2.95, 35.44) * mm, "mid": v(3.52, 35.62) * mm, "end": v(3.8, 36.14) * mm});
            skLineSegment(sketch, "E14.29.1", {"start": v(3.98, 37.9) * mm, "end": v(3.8, 36.14) * mm});
            skArc(sketch, "E14.29.2", {"start": v(3.98, 37.9) * mm, "mid": v(4.62, 38.96) * mm, "end": v(5.4, 39.95) * mm});
            skArc(sketch, "E14.29.3", {"start": v(6.06, 40.2) * mm, "mid": v(5.7, 40.15) * mm, "end": v(5.4, 39.95) * mm});
            skLineSegment(sketch, "E14.29.4", {"start": v(6.06, 40.2) * mm, "end": v(6.36, 40.17) * mm});
            skLineSegment(sketch, "E14.29.5", {"start": v(6.66, 40.1) * mm, "end": v(6.36, 40.17) * mm});
            skArc(sketch, "E14.29.6", {"start": v(7.21, 39.66) * mm, "mid": v(6.99, 39.95) * mm, "end": v(6.66, 40.1) * mm});
            skArc(sketch, "E14.29.7", {"start": v(7.92, 37.27) * mm, "mid": v(7.64, 38.49) * mm, "end": v(7.21, 39.66) * mm});
            skLineSegment(sketch, "E14.29.8", {"start": v(7.92, 37.27) * mm, "end": v(7.56, 35.54) * mm});
            skArc(sketch, "E14.29.9", {"start": v(7.56, 35.54) * mm, "mid": v(7.66, 34.96) * mm, "end": v(8.15, 34.61) * mm});
            skSolve(sketch);
        }
        {
            var Q0;
            Q0 = qSketchRegion(id + "F0", true);
            extrude(context, id + "F1", {"entities" : qUnion([Q0]), "depth" : 114.3 * mm});
        }
        {
            var Q0;
            Q0=makeQuery(id+"F1.opExtrude","CAP_FACE",FACE,{"disambiguationData":[OSD([sQuery(id+"F0.wireOp",EDGE,"E0"),sQuery(id+"F0.wireOp",EDGE,"E2"),sQuery(id+"F0.wireOp",EDGE,"E3"),sQuery(id+"F0.wireOp",EDGE,"E4.trimOffspring"),sQuery(id+"F0.wireOp",EDGE,"E5.MirrorCS"),sQuery(id+"F0.wireOp",EDGE,"E6.MirrorCS"),sQuery(id+"F0.wireOp",EDGE,"E7.MirrorCS"),sQuery(id+"F0.wireOp",EDGE,"E10.filletArc"),sQuery(id+"F0.wireOp",EDGE,"E11.filletArc"),sQuery(id+"F0.wireOp",EDGE,"E12.filletArc"),sQuery(id+"F0.wireOp",EDGE,"E13.filletArc"),sQuery(id+"F0.wireOp",EDGE,"E14.1.0"),sQuery(id+"F0.wireOp",EDGE,"E14.1.1"),sQuery(id+"F0.wireOp",EDGE,"E14.1.2"),sQuery(id+"F0.wireOp",EDGE,"E14.1.3"),sQuery(id+"F0.wireOp",EDGE,"E14.1.4"),sQuery(id+"F0.wireOp",EDGE,"E14.1.5"),sQuery(id+"F0.wireOp",EDGE,"E14.1.6"),sQuery(id+"F0.wireOp",EDGE,"E14.1.7"),sQuery(id+"F0.wireOp",EDGE,"E14.1.8"),sQuery(id+"F0.wireOp",EDGE,"E14.1.9"),sQuery(id+"F0.wireOp",EDGE,"E14.2.0"),sQuery(id+"F0.wireOp",EDGE,"E14.2.1"),sQuery(id+"F0.wireOp",EDGE,"E14.2.2"),sQuery(id+"F0.wireOp",EDGE,"E14.2.3"),sQuery(id+"F0.wireOp",EDGE,"E14.2.4"),sQuery(id+"F0.wireOp",EDGE,"E14.2.5"),sQuery(id+"F0.wireOp",EDGE,"E14.2.6"),sQuery(id+"F0.wireOp",EDGE,"E14.2.7"),sQuery(id+"F0.wireOp",EDGE,"E14.2.8"),sQuery(id+"F0.wireOp",EDGE,"E14.2.9"),sQuery(id+"F0.wireOp",EDGE,"E14.3.0"),sQuery(id+"F0.wireOp",EDGE,"E14.3.1"),sQuery(id+"F0.wireOp",EDGE,"E14.3.2"),sQuery(id+"F0.wireOp",EDGE,"E14.3.3"),sQuery(id+"F0.wireOp",EDGE,"E14.3.4"),sQuery(id+"F0.wireOp",EDGE,"E14.3.5"),sQuery(id+"F0.wireOp",EDGE,"E14.3.6"),sQuery(id+"F0.wireOp",EDGE,"E14.3.7"),sQuery(id+"F0.wireOp",EDGE,"E14.3.8"),sQuery(id+"F0.wireOp",EDGE,"E14.3.9"),sQuery(id+"F0.wireOp",EDGE,"E14.4.0"),sQuery(id+"F0.wireOp",EDGE,"E14.4.1"),sQuery(id+"F0.wireOp",EDGE,"E14.4.2"),sQuery(id+"F0.wireOp",EDGE,"E14.4.3"),sQuery(id+"F0.wireOp",EDGE,"E14.4.4"),sQuery(id+"F0.wireOp",EDGE,"E14.4.5"),sQuery(id+"F0.wireOp",EDGE,"E14.4.6"),sQuery(id+"F0.wireOp",EDGE,"E14.4.7"),sQuery(id+"F0.wireOp",EDGE,"E14.4.8"),sQuery(id+"F0.wireOp",EDGE,"E14.4.9"),sQuery(id+"F0.wireOp",EDGE,"E14.5.0"),sQuery(id+"F0.wireOp",EDGE,"E14.5.1"),sQuery(id+"F0.wireOp",EDGE,"E14.5.2"),sQuery(id+"F0.wireOp",EDGE,"E14.5.3"),sQuery(id+"F0.wireOp",EDGE,"E14.5.4"),sQuery(id+"F0.wireOp",EDGE,"E14.5.5"),sQuery(id+"F0.wireOp",EDGE,"E14.5.6"),sQuery(id+"F0.wireOp",EDGE,"E14.5.7"),sQuery(id+"F0.wireOp",EDGE,"E14.5.8"),sQuery(id+"F0.wireOp",EDGE,"E14.5.9"),sQuery(id+"F0.wireOp",EDGE,"E14.6.0"),sQuery(id+"F0.wireOp",EDGE,"E14.6.1"),sQuery(id+"F0.wireOp",EDGE,"E14.6.2"),sQuery(id+"F0.wireOp",EDGE,"E14.6.3"),sQuery(id+"F0.wireOp",EDGE,"E14.6.4"),sQuery(id+"F0.wireOp",EDGE,"E14.6.5"),sQuery(id+"F0.wireOp",EDGE,"E14.6.6"),sQuery(id+"F0.wireOp",EDGE,"E14.6.7"),sQuery(id+"F0.wireOp",EDGE,"E14.6.8"),sQuery(id+"F0.wireOp",EDGE,"E14.6.9"),sQuery(id+"F0.wireOp",EDGE,"E14.7.0"),sQuery(id+"F0.wireOp",EDGE,"E14.7.1"),sQuery(id+"F0.wireOp",EDGE,"E14.7.2"),sQuery(id+"F0.wireOp",EDGE,"E14.7.3"),sQuery(id+"F0.wireOp",EDGE,"E14.7.4"),sQuery(id+"F0.wireOp",EDGE,"E14.7.5"),sQuery(id+"F0.wireOp",EDGE,"E14.7.6"),sQuery(id+"F0.wireOp",EDGE,"E14.7.7"),sQuery(id+"F0.wireOp",EDGE,"E14.7.8"),sQuery(id+"F0.wireOp",EDGE,"E14.7.9"),sQuery(id+"F0.wireOp",EDGE,"E14.8.0"),sQuery(id+"F0.wireOp",EDGE,"E14.8.1"),sQuery(id+"F0.wireOp",EDGE,"E14.8.2"),sQuery(id+"F0.wireOp",EDGE,"E14.8.3"),sQuery(id+"F0.wireOp",EDGE,"E14.8.4"),sQuery(id+"F0.wireOp",EDGE,"E14.8.5"),sQuery(id+"F0.wireOp",EDGE,"E14.8.6"),sQuery(id+"F0.wireOp",EDGE,"E14.8.7"),sQuery(id+"F0.wireOp",EDGE,"E14.8.8"),sQuery(id+"F0.wireOp",EDGE,"E14.8.9"),sQuery(id+"F0.wireOp",EDGE,"E14.9.0"),sQuery(id+"F0.wireOp",EDGE,"E14.9.1"),sQuery(id+"F0.wireOp",EDGE,"E14.9.2"),sQuery(id+"F0.wireOp",EDGE,"E14.9.3"),sQuery(id+"F0.wireOp",EDGE,"E14.9.4"),sQuery(id+"F0.wireOp",EDGE,"E14.9.5"),sQuery(id+"F0.wireOp",EDGE,"E14.9.6"),sQuery(id+"F0.wireOp",EDGE,"E14.9.7"),sQuery(id+"F0.wireOp",EDGE,"E14.9.8"),sQuery(id+"F0.wireOp",EDGE,"E14.9.9"),sQuery(id+"F0.wireOp",EDGE,"E14.10.0"),sQuery(id+"F0.wireOp",EDGE,"E14.10.1"),sQuery(id+"F0.wireOp",EDGE,"E14.10.2"),sQuery(id+"F0.wireOp",EDGE,"E14.10.3"),sQuery(id+"F0.wireOp",EDGE,"E14.10.4"),sQuery(id+"F0.wireOp",EDGE,"E14.10.5"),sQuery(id+"F0.wireOp",EDGE,"E14.10.6"),sQuery(id+"F0.wireOp",EDGE,"E14.10.7"),sQuery(id+"F0.wireOp",EDGE,"E14.10.8"),sQuery(id+"F0.wireOp",EDGE,"E14.10.9"),sQuery(id+"F0.wireOp",EDGE,"E14.11.0"),sQuery(id+"F0.wireOp",EDGE,"E14.11.1"),sQuery(id+"F0.wireOp",EDGE,"E14.11.2"),sQuery(id+"F0.wireOp",EDGE,"E14.11.3"),sQuery(id+"F0.wireOp",EDGE,"E14.11.4"),sQuery(id+"F0.wireOp",EDGE,"E14.11.5"),sQuery(id+"F0.wireOp",EDGE,"E14.11.6"),sQuery(id+"F0.wireOp",EDGE,"E14.11.7"),sQuery(id+"F0.wireOp",EDGE,"E14.11.8"),sQuery(id+"F0.wireOp",EDGE,"E14.11.9"),sQuery(id+"F0.wireOp",EDGE,"E14.12.0"),sQuery(id+"F0.wireOp",EDGE,"E14.12.1"),sQuery(id+"F0.wireOp",EDGE,"E14.12.2"),sQuery(id+"F0.wireOp",EDGE,"E14.12.3"),sQuery(id+"F0.wireOp",EDGE,"E14.12.4"),sQuery(id+"F0.wireOp",EDGE,"E14.12.5"),sQuery(id+"F0.wireOp",EDGE,"E14.12.6"),sQuery(id+"F0.wireOp",EDGE,"E14.12.7"),sQuery(id+"F0.wireOp",EDGE,"E14.12.8"),sQuery(id+"F0.wireOp",EDGE,"E14.12.9"),sQuery(id+"F0.wireOp",EDGE,"E14.13.0"),sQuery(id+"F0.wireOp",EDGE,"E14.13.1"),sQuery(id+"F0.wireOp",EDGE,"E14.13.2"),sQuery(id+"F0.wireOp",EDGE,"E14.13.3"),sQuery(id+"F0.wireOp",EDGE,"E14.13.4"),sQuery(id+"F0.wireOp",EDGE,"E14.13.5"),sQuery(id+"F0.wireOp",EDGE,"E14.13.6"),sQuery(id+"F0.wireOp",EDGE,"E14.13.7"),sQuery(id+"F0.wireOp",EDGE,"E14.13.8"),sQuery(id+"F0.wireOp",EDGE,"E14.13.9"),sQuery(id+"F0.wireOp",EDGE,"E14.14.0"),sQuery(id+"F0.wireOp",EDGE,"E14.14.1"),sQuery(id+"F0.wireOp",EDGE,"E14.14.2"),sQuery(id+"F0.wireOp",EDGE,"E14.14.3"),sQuery(id+"F0.wireOp",EDGE,"E14.14.4"),sQuery(id+"F0.wireOp",EDGE,"E14.14.5"),sQuery(id+"F0.wireOp",EDGE,"E14.14.6"),sQuery(id+"F0.wireOp",EDGE,"E14.14.7"),sQuery(id+"F0.wireOp",EDGE,"E14.14.8"),sQuery(id+"F0.wireOp",EDGE,"E14.14.9"),sQuery(id+"F0.wireOp",EDGE,"E14.15.0"),sQuery(id+"F0.wireOp",EDGE,"E14.15.1"),sQuery(id+"F0.wireOp",EDGE,"E14.15.2"),sQuery(id+"F0.wireOp",EDGE,"E14.15.3"),sQuery(id+"F0.wireOp",EDGE,"E14.15.4"),sQuery(id+"F0.wireOp",EDGE,"E14.15.5"),sQuery(id+"F0.wireOp",EDGE,"E14.15.6"),sQuery(id+"F0.wireOp",EDGE,"E14.15.7"),sQuery(id+"F0.wireOp",EDGE,"E14.15.8"),sQuery(id+"F0.wireOp",EDGE,"E14.15.9"),sQuery(id+"F0.wireOp",EDGE,"E14.16.0"),sQuery(id+"F0.wireOp",EDGE,"E14.16.1"),sQuery(id+"F0.wireOp",EDGE,"E14.16.2"),sQuery(id+"F0.wireOp",EDGE,"E14.16.3"),sQuery(id+"F0.wireOp",EDGE,"E14.16.4"),sQuery(id+"F0.wireOp",EDGE,"E14.16.5"),sQuery(id+"F0.wireOp",EDGE,"E14.16.6"),sQuery(id+"F0.wireOp",EDGE,"E14.16.7"),sQuery(id+"F0.wireOp",EDGE,"E14.16.8"),sQuery(id+"F0.wireOp",EDGE,"E14.16.9"),sQuery(id+"F0.wireOp",EDGE,"E14.17.0"),sQuery(id+"F0.wireOp",EDGE,"E14.17.1"),sQuery(id+"F0.wireOp",EDGE,"E14.17.2"),sQuery(id+"F0.wireOp",EDGE,"E14.17.3"),sQuery(id+"F0.wireOp",EDGE,"E14.17.4"),sQuery(id+"F0.wireOp",EDGE,"E14.17.5"),sQuery(id+"F0.wireOp",EDGE,"E14.17.6"),sQuery(id+"F0.wireOp",EDGE,"E14.17.7"),sQuery(id+"F0.wireOp",EDGE,"E14.17.8"),sQuery(id+"F0.wireOp",EDGE,"E14.17.9"),sQuery(id+"F0.wireOp",EDGE,"E14.18.0"),sQuery(id+"F0.wireOp",EDGE,"E14.18.1"),sQuery(id+"F0.wireOp",EDGE,"E14.18.2"),sQuery(id+"F0.wireOp",EDGE,"E14.18.3"),sQuery(id+"F0.wireOp",EDGE,"E14.18.4"),sQuery(id+"F0.wireOp",EDGE,"E14.18.5"),sQuery(id+"F0.wireOp",EDGE,"E14.18.6"),sQuery(id+"F0.wireOp",EDGE,"E14.18.7"),sQuery(id+"F0.wireOp",EDGE,"E14.18.8"),sQuery(id+"F0.wireOp",EDGE,"E14.18.9"),sQuery(id+"F0.wireOp",EDGE,"E14.19.0"),sQuery(id+"F0.wireOp",EDGE,"E14.19.1"),sQuery(id+"F0.wireOp",EDGE,"E14.19.2"),sQuery(id+"F0.wireOp",EDGE,"E14.19.3"),sQuery(id+"F0.wireOp",EDGE,"E14.19.4"),sQuery(id+"F0.wireOp",EDGE,"E14.19.5"),sQuery(id+"F0.wireOp",EDGE,"E14.19.6"),sQuery(id+"F0.wireOp",EDGE,"E14.19.7"),sQuery(id+"F0.wireOp",EDGE,"E14.19.8"),sQuery(id+"F0.wireOp",EDGE,"E14.19.9"),sQuery(id+"F0.wireOp",EDGE,"E14.20.0"),sQuery(id+"F0.wireOp",EDGE,"E14.20.1"),sQuery(id+"F0.wireOp",EDGE,"E14.20.2"),sQuery(id+"F0.wireOp",EDGE,"E14.20.3"),sQuery(id+"F0.wireOp",EDGE,"E14.20.4"),sQuery(id+"F0.wireOp",EDGE,"E14.20.5"),sQuery(id+"F0.wireOp",EDGE,"E14.20.6"),sQuery(id+"F0.wireOp",EDGE,"E14.20.7"),sQuery(id+"F0.wireOp",EDGE,"E14.20.8"),sQuery(id+"F0.wireOp",EDGE,"E14.20.9"),sQuery(id+"F0.wireOp",EDGE,"E14.21.0"),sQuery(id+"F0.wireOp",EDGE,"E14.21.1"),sQuery(id+"F0.wireOp",EDGE,"E14.21.2"),sQuery(id+"F0.wireOp",EDGE,"E14.21.3"),sQuery(id+"F0.wireOp",EDGE,"E14.21.4"),sQuery(id+"F0.wireOp",EDGE,"E14.21.5"),sQuery(id+"F0.wireOp",EDGE,"E14.21.6"),sQuery(id+"F0.wireOp",EDGE,"E14.21.7"),sQuery(id+"F0.wireOp",EDGE,"E14.21.8"),sQuery(id+"F0.wireOp",EDGE,"E14.21.9"),sQuery(id+"F0.wireOp",EDGE,"E14.22.0"),sQuery(id+"F0.wireOp",EDGE,"E14.22.1"),sQuery(id+"F0.wireOp",EDGE,"E14.22.2"),sQuery(id+"F0.wireOp",EDGE,"E14.22.3"),sQuery(id+"F0.wireOp",EDGE,"E14.22.4"),sQuery(id+"F0.wireOp",EDGE,"E14.22.5"),sQuery(id+"F0.wireOp",EDGE,"E14.22.6"),sQuery(id+"F0.wireOp",EDGE,"E14.22.7"),sQuery(id+"F0.wireOp",EDGE,"E14.22.8"),sQuery(id+"F0.wireOp",EDGE,"E14.22.9"),sQuery(id+"F0.wireOp",EDGE,"E14.23.0"),sQuery(id+"F0.wireOp",EDGE,"E14.23.1"),sQuery(id+"F0.wireOp",EDGE,"E14.23.2"),sQuery(id+"F0.wireOp",EDGE,"E14.23.3"),sQuery(id+"F0.wireOp",EDGE,"E14.23.4"),sQuery(id+"F0.wireOp",EDGE,"E14.23.5"),sQuery(id+"F0.wireOp",EDGE,"E14.23.6"),sQuery(id+"F0.wireOp",EDGE,"E14.23.7"),sQuery(id+"F0.wireOp",EDGE,"E14.23.8"),sQuery(id+"F0.wireOp",EDGE,"E14.23.9"),sQuery(id+"F0.wireOp",EDGE,"E14.24.0"),sQuery(id+"F0.wireOp",EDGE,"E14.24.1"),sQuery(id+"F0.wireOp",EDGE,"E14.24.2"),sQuery(id+"F0.wireOp",EDGE,"E14.24.3"),sQuery(id+"F0.wireOp",EDGE,"E14.24.4"),sQuery(id+"F0.wireOp",EDGE,"E14.24.5"),sQuery(id+"F0.wireOp",EDGE,"E14.24.6"),sQuery(id+"F0.wireOp",EDGE,"E14.24.7"),sQuery(id+"F0.wireOp",EDGE,"E14.24.8"),sQuery(id+"F0.wireOp",EDGE,"E14.24.9"),sQuery(id+"F0.wireOp",EDGE,"E14.25.0"),sQuery(id+"F0.wireOp",EDGE,"E14.25.1"),sQuery(id+"F0.wireOp",EDGE,"E14.25.2"),sQuery(id+"F0.wireOp",EDGE,"E14.25.3"),sQuery(id+"F0.wireOp",EDGE,"E14.25.4"),sQuery(id+"F0.wireOp",EDGE,"E14.25.5"),sQuery(id+"F0.wireOp",EDGE,"E14.25.6"),sQuery(id+"F0.wireOp",EDGE,"E14.25.7"),sQuery(id+"F0.wireOp",EDGE,"E14.25.8"),sQuery(id+"F0.wireOp",EDGE,"E14.25.9"),sQuery(id+"F0.wireOp",EDGE,"E14.26.0"),sQuery(id+"F0.wireOp",EDGE,"E14.26.1"),sQuery(id+"F0.wireOp",EDGE,"E14.26.2"),sQuery(id+"F0.wireOp",EDGE,"E14.26.3"),sQuery(id+"F0.wireOp",EDGE,"E14.26.4"),sQuery(id+"F0.wireOp",EDGE,"E14.26.5"),sQuery(id+"F0.wireOp",EDGE,"E14.26.6"),sQuery(id+"F0.wireOp",EDGE,"E14.26.7"),sQuery(id+"F0.wireOp",EDGE,"E14.26.8"),sQuery(id+"F0.wireOp",EDGE,"E14.26.9"),sQuery(id+"F0.wireOp",EDGE,"E14.27.0"),sQuery(id+"F0.wireOp",EDGE,"E14.27.1"),sQuery(id+"F0.wireOp",EDGE,"E14.27.2"),sQuery(id+"F0.wireOp",EDGE,"E14.27.3"),sQuery(id+"F0.wireOp",EDGE,"E14.27.4"),sQuery(id+"F0.wireOp",EDGE,"E14.27.5"),sQuery(id+"F0.wireOp",EDGE,"E14.27.6"),sQuery(id+"F0.wireOp",EDGE,"E14.27.7"),sQuery(id+"F0.wireOp",EDGE,"E14.27.8"),sQuery(id+"F0.wireOp",EDGE,"E14.27.9"),sQuery(id+"F0.wireOp",EDGE,"E14.28.0"),sQuery(id+"F0.wireOp",EDGE,"E14.28.1"),sQuery(id+"F0.wireOp",EDGE,"E14.28.2"),sQuery(id+"F0.wireOp",EDGE,"E14.28.3"),sQuery(id+"F0.wireOp",EDGE,"E14.28.4"),sQuery(id+"F0.wireOp",EDGE,"E14.28.5"),sQuery(id+"F0.wireOp",EDGE,"E14.28.6"),sQuery(id+"F0.wireOp",EDGE,"E14.28.7"),sQuery(id+"F0.wireOp",EDGE,"E14.28.8"),sQuery(id+"F0.wireOp",EDGE,"E14.28.9"),sQuery(id+"F0.wireOp",EDGE,"E14.29.0"),sQuery(id+"F0.wireOp",EDGE,"E14.29.1"),sQuery(id+"F0.wireOp",EDGE,"E14.29.2"),sQuery(id+"F0.wireOp",EDGE,"E14.29.3"),sQuery(id+"F0.wireOp",EDGE,"E14.29.4"),sQuery(id+"F0.wireOp",EDGE,"E14.29.5"),sQuery(id+"F0.wireOp",EDGE,"E14.29.6"),sQuery(id+"F0.wireOp",EDGE,"E14.29.7"),sQuery(id+"F0.wireOp",EDGE,"E14.29.8"),sQuery(id+"F0.wireOp",EDGE,"E14.29.9")])],"isStart":false});
            var sketch = newSketch(context, id + "F2", { "sketchPlane" : qUnion([Q0])});
            skCircle(sketch, "E15", {"center": v(0, 0) * mm, "radius": 12.7 * mm});
            skCircle(sketch, "E16", {"center": v(0, 0) * mm, "radius": 6.35 * mm});
            skSolve(sketch);
        }
        {
            var Q0;
            Q0 = qSketchRegion(id + "F2", true);
            extrude(context, id + "F3", {"entities" : qUnion([Q0]), "operationType" : NewBodyOperationType.ADD, "depth" : 12.7 * mm});
        }
        {
            var Q0;
            Q0=makeQuery(id+"F3.boolean.opBoolean","SPLIT",FACE,{"disambiguationData":[TD([makeQuery(id+"F3.opExtrude","SWEPT_FACE",FACE,{"disambiguationData":[OSD([sQuery(id+"F2.wireOp",EDGE,"E16")])]})])],"derivedFrom":makeQuery(id+"F1.opExtrude","CAP_FACE",FACE,{"disambiguationData":[OSD([sQuery(id+"F0.wireOp",EDGE,"E0"),sQuery(id+"F0.wireOp",EDGE,"E2"),sQuery(id+"F0.wireOp",EDGE,"E3"),sQuery(id+"F0.wireOp",EDGE,"E4.trimOffspring"),sQuery(id+"F0.wireOp",EDGE,"E5.MirrorCS"),sQuery(id+"F0.wireOp",EDGE,"E6.MirrorCS"),sQuery(id+"F0.wireOp",EDGE,"E7.MirrorCS"),sQuery(id+"F0.wireOp",EDGE,"E10.filletArc"),sQuery(id+"F0.wireOp",EDGE,"E11.filletArc"),sQuery(id+"F0.wireOp",EDGE,"E12.filletArc"),sQuery(id+"F0.wireOp",EDGE,"E13.filletArc"),sQuery(id+"F0.wireOp",EDGE,"E14.1.0"),sQuery(id+"F0.wireOp",EDGE,"E14.1.1"),sQuery(id+"F0.wireOp",EDGE,"E14.1.2"),sQuery(id+"F0.wireOp",EDGE,"E14.1.3"),sQuery(id+"F0.wireOp",EDGE,"E14.1.4"),sQuery(id+"F0.wireOp",EDGE,"E14.1.5"),sQuery(id+"F0.wireOp",EDGE,"E14.1.6"),sQuery(id+"F0.wireOp",EDGE,"E14.1.7"),sQuery(id+"F0.wireOp",EDGE,"E14.1.8"),sQuery(id+"F0.wireOp",EDGE,"E14.1.9"),sQuery(id+"F0.wireOp",EDGE,"E14.2.0"),sQuery(id+"F0.wireOp",EDGE,"E14.2.1"),sQuery(id+"F0.wireOp",EDGE,"E14.2.2"),sQuery(id+"F0.wireOp",EDGE,"E14.2.3"),sQuery(id+"F0.wireOp",EDGE,"E14.2.4"),sQuery(id+"F0.wireOp",EDGE,"E14.2.5"),sQuery(id+"F0.wireOp",EDGE,"E14.2.6"),sQuery(id+"F0.wireOp",EDGE,"E14.2.7"),sQuery(id+"F0.wireOp",EDGE,"E14.2.8"),sQuery(id+"F0.wireOp",EDGE,"E14.2.9"),sQuery(id+"F0.wireOp",EDGE,"E14.3.0"),sQuery(id+"F0.wireOp",EDGE,"E14.3.1"),sQuery(id+"F0.wireOp",EDGE,"E14.3.2"),sQuery(id+"F0.wireOp",EDGE,"E14.3.3"),sQuery(id+"F0.wireOp",EDGE,"E14.3.4"),sQuery(id+"F0.wireOp",EDGE,"E14.3.5"),sQuery(id+"F0.wireOp",EDGE,"E14.3.6"),sQuery(id+"F0.wireOp",EDGE,"E14.3.7"),sQuery(id+"F0.wireOp",EDGE,"E14.3.8"),sQuery(id+"F0.wireOp",EDGE,"E14.3.9"),sQuery(id+"F0.wireOp",EDGE,"E14.4.0"),sQuery(id+"F0.wireOp",EDGE,"E14.4.1"),sQuery(id+"F0.wireOp",EDGE,"E14.4.2"),sQuery(id+"F0.wireOp",EDGE,"E14.4.3"),sQuery(id+"F0.wireOp",EDGE,"E14.4.4"),sQuery(id+"F0.wireOp",EDGE,"E14.4.5"),sQuery(id+"F0.wireOp",EDGE,"E14.4.6"),sQuery(id+"F0.wireOp",EDGE,"E14.4.7"),sQuery(id+"F0.wireOp",EDGE,"E14.4.8"),sQuery(id+"F0.wireOp",EDGE,"E14.4.9"),sQuery(id+"F0.wireOp",EDGE,"E14.5.0"),sQuery(id+"F0.wireOp",EDGE,"E14.5.1"),sQuery(id+"F0.wireOp",EDGE,"E14.5.2"),sQuery(id+"F0.wireOp",EDGE,"E14.5.3"),sQuery(id+"F0.wireOp",EDGE,"E14.5.4"),sQuery(id+"F0.wireOp",EDGE,"E14.5.5"),sQuery(id+"F0.wireOp",EDGE,"E14.5.6"),sQuery(id+"F0.wireOp",EDGE,"E14.5.7"),sQuery(id+"F0.wireOp",EDGE,"E14.5.8"),sQuery(id+"F0.wireOp",EDGE,"E14.5.9"),sQuery(id+"F0.wireOp",EDGE,"E14.6.0"),sQuery(id+"F0.wireOp",EDGE,"E14.6.1"),sQuery(id+"F0.wireOp",EDGE,"E14.6.2"),sQuery(id+"F0.wireOp",EDGE,"E14.6.3"),sQuery(id+"F0.wireOp",EDGE,"E14.6.4"),sQuery(id+"F0.wireOp",EDGE,"E14.6.5"),sQuery(id+"F0.wireOp",EDGE,"E14.6.6"),sQuery(id+"F0.wireOp",EDGE,"E14.6.7"),sQuery(id+"F0.wireOp",EDGE,"E14.6.8"),sQuery(id+"F0.wireOp",EDGE,"E14.6.9"),sQuery(id+"F0.wireOp",EDGE,"E14.7.0"),sQuery(id+"F0.wireOp",EDGE,"E14.7.1"),sQuery(id+"F0.wireOp",EDGE,"E14.7.2"),sQuery(id+"F0.wireOp",EDGE,"E14.7.3"),sQuery(id+"F0.wireOp",EDGE,"E14.7.4"),sQuery(id+"F0.wireOp",EDGE,"E14.7.5"),sQuery(id+"F0.wireOp",EDGE,"E14.7.6"),sQuery(id+"F0.wireOp",EDGE,"E14.7.7"),sQuery(id+"F0.wireOp",EDGE,"E14.7.8"),sQuery(id+"F0.wireOp",EDGE,"E14.7.9"),sQuery(id+"F0.wireOp",EDGE,"E14.8.0"),sQuery(id+"F0.wireOp",EDGE,"E14.8.1"),sQuery(id+"F0.wireOp",EDGE,"E14.8.2"),sQuery(id+"F0.wireOp",EDGE,"E14.8.3"),sQuery(id+"F0.wireOp",EDGE,"E14.8.4"),sQuery(id+"F0.wireOp",EDGE,"E14.8.5"),sQuery(id+"F0.wireOp",EDGE,"E14.8.6"),sQuery(id+"F0.wireOp",EDGE,"E14.8.7"),sQuery(id+"F0.wireOp",EDGE,"E14.8.8"),sQuery(id+"F0.wireOp",EDGE,"E14.8.9"),sQuery(id+"F0.wireOp",EDGE,"E14.9.0"),sQuery(id+"F0.wireOp",EDGE,"E14.9.1"),sQuery(id+"F0.wireOp",EDGE,"E14.9.2"),sQuery(id+"F0.wireOp",EDGE,"E14.9.3"),sQuery(id+"F0.wireOp",EDGE,"E14.9.4"),sQuery(id+"F0.wireOp",EDGE,"E14.9.5"),sQuery(id+"F0.wireOp",EDGE,"E14.9.6"),sQuery(id+"F0.wireOp",EDGE,"E14.9.7"),sQuery(id+"F0.wireOp",EDGE,"E14.9.8"),sQuery(id+"F0.wireOp",EDGE,"E14.9.9"),sQuery(id+"F0.wireOp",EDGE,"E14.10.0"),sQuery(id+"F0.wireOp",EDGE,"E14.10.1"),sQuery(id+"F0.wireOp",EDGE,"E14.10.2"),sQuery(id+"F0.wireOp",EDGE,"E14.10.3"),sQuery(id+"F0.wireOp",EDGE,"E14.10.4"),sQuery(id+"F0.wireOp",EDGE,"E14.10.5"),sQuery(id+"F0.wireOp",EDGE,"E14.10.6"),sQuery(id+"F0.wireOp",EDGE,"E14.10.7"),sQuery(id+"F0.wireOp",EDGE,"E14.10.8"),sQuery(id+"F0.wireOp",EDGE,"E14.10.9"),sQuery(id+"F0.wireOp",EDGE,"E14.11.0"),sQuery(id+"F0.wireOp",EDGE,"E14.11.1"),sQuery(id+"F0.wireOp",EDGE,"E14.11.2"),sQuery(id+"F0.wireOp",EDGE,"E14.11.3"),sQuery(id+"F0.wireOp",EDGE,"E14.11.4"),sQuery(id+"F0.wireOp",EDGE,"E14.11.5"),sQuery(id+"F0.wireOp",EDGE,"E14.11.6"),sQuery(id+"F0.wireOp",EDGE,"E14.11.7"),sQuery(id+"F0.wireOp",EDGE,"E14.11.8"),sQuery(id+"F0.wireOp",EDGE,"E14.11.9"),sQuery(id+"F0.wireOp",EDGE,"E14.12.0"),sQuery(id+"F0.wireOp",EDGE,"E14.12.1"),sQuery(id+"F0.wireOp",EDGE,"E14.12.2"),sQuery(id+"F0.wireOp",EDGE,"E14.12.3"),sQuery(id+"F0.wireOp",EDGE,"E14.12.4"),sQuery(id+"F0.wireOp",EDGE,"E14.12.5"),sQuery(id+"F0.wireOp",EDGE,"E14.12.6"),sQuery(id+"F0.wireOp",EDGE,"E14.12.7"),sQuery(id+"F0.wireOp",EDGE,"E14.12.8"),sQuery(id+"F0.wireOp",EDGE,"E14.12.9"),sQuery(id+"F0.wireOp",EDGE,"E14.13.0"),sQuery(id+"F0.wireOp",EDGE,"E14.13.1"),sQuery(id+"F0.wireOp",EDGE,"E14.13.2"),sQuery(id+"F0.wireOp",EDGE,"E14.13.3"),sQuery(id+"F0.wireOp",EDGE,"E14.13.4"),sQuery(id+"F0.wireOp",EDGE,"E14.13.5"),sQuery(id+"F0.wireOp",EDGE,"E14.13.6"),sQuery(id+"F0.wireOp",EDGE,"E14.13.7"),sQuery(id+"F0.wireOp",EDGE,"E14.13.8"),sQuery(id+"F0.wireOp",EDGE,"E14.13.9"),sQuery(id+"F0.wireOp",EDGE,"E14.14.0"),sQuery(id+"F0.wireOp",EDGE,"E14.14.1"),sQuery(id+"F0.wireOp",EDGE,"E14.14.2"),sQuery(id+"F0.wireOp",EDGE,"E14.14.3"),sQuery(id+"F0.wireOp",EDGE,"E14.14.4"),sQuery(id+"F0.wireOp",EDGE,"E14.14.5"),sQuery(id+"F0.wireOp",EDGE,"E14.14.6"),sQuery(id+"F0.wireOp",EDGE,"E14.14.7"),sQuery(id+"F0.wireOp",EDGE,"E14.14.8"),sQuery(id+"F0.wireOp",EDGE,"E14.14.9"),sQuery(id+"F0.wireOp",EDGE,"E14.15.0"),sQuery(id+"F0.wireOp",EDGE,"E14.15.1"),sQuery(id+"F0.wireOp",EDGE,"E14.15.2"),sQuery(id+"F0.wireOp",EDGE,"E14.15.3"),sQuery(id+"F0.wireOp",EDGE,"E14.15.4"),sQuery(id+"F0.wireOp",EDGE,"E14.15.5"),sQuery(id+"F0.wireOp",EDGE,"E14.15.6"),sQuery(id+"F0.wireOp",EDGE,"E14.15.7"),sQuery(id+"F0.wireOp",EDGE,"E14.15.8"),sQuery(id+"F0.wireOp",EDGE,"E14.15.9"),sQuery(id+"F0.wireOp",EDGE,"E14.16.0"),sQuery(id+"F0.wireOp",EDGE,"E14.16.1"),sQuery(id+"F0.wireOp",EDGE,"E14.16.2"),sQuery(id+"F0.wireOp",EDGE,"E14.16.3"),sQuery(id+"F0.wireOp",EDGE,"E14.16.4"),sQuery(id+"F0.wireOp",EDGE,"E14.16.5"),sQuery(id+"F0.wireOp",EDGE,"E14.16.6"),sQuery(id+"F0.wireOp",EDGE,"E14.16.7"),sQuery(id+"F0.wireOp",EDGE,"E14.16.8"),sQuery(id+"F0.wireOp",EDGE,"E14.16.9"),sQuery(id+"F0.wireOp",EDGE,"E14.17.0"),sQuery(id+"F0.wireOp",EDGE,"E14.17.1"),sQuery(id+"F0.wireOp",EDGE,"E14.17.2"),sQuery(id+"F0.wireOp",EDGE,"E14.17.3"),sQuery(id+"F0.wireOp",EDGE,"E14.17.4"),sQuery(id+"F0.wireOp",EDGE,"E14.17.5"),sQuery(id+"F0.wireOp",EDGE,"E14.17.6"),sQuery(id+"F0.wireOp",EDGE,"E14.17.7"),sQuery(id+"F0.wireOp",EDGE,"E14.17.8"),sQuery(id+"F0.wireOp",EDGE,"E14.17.9"),sQuery(id+"F0.wireOp",EDGE,"E14.18.0"),sQuery(id+"F0.wireOp",EDGE,"E14.18.1"),sQuery(id+"F0.wireOp",EDGE,"E14.18.2"),sQuery(id+"F0.wireOp",EDGE,"E14.18.3"),sQuery(id+"F0.wireOp",EDGE,"E14.18.4"),sQuery(id+"F0.wireOp",EDGE,"E14.18.5"),sQuery(id+"F0.wireOp",EDGE,"E14.18.6"),sQuery(id+"F0.wireOp",EDGE,"E14.18.7"),sQuery(id+"F0.wireOp",EDGE,"E14.18.8"),sQuery(id+"F0.wireOp",EDGE,"E14.18.9"),sQuery(id+"F0.wireOp",EDGE,"E14.19.0"),sQuery(id+"F0.wireOp",EDGE,"E14.19.1"),sQuery(id+"F0.wireOp",EDGE,"E14.19.2"),sQuery(id+"F0.wireOp",EDGE,"E14.19.3"),sQuery(id+"F0.wireOp",EDGE,"E14.19.4"),sQuery(id+"F0.wireOp",EDGE,"E14.19.5"),sQuery(id+"F0.wireOp",EDGE,"E14.19.6"),sQuery(id+"F0.wireOp",EDGE,"E14.19.7"),sQuery(id+"F0.wireOp",EDGE,"E14.19.8"),sQuery(id+"F0.wireOp",EDGE,"E14.19.9"),sQuery(id+"F0.wireOp",EDGE,"E14.20.0"),sQuery(id+"F0.wireOp",EDGE,"E14.20.1"),sQuery(id+"F0.wireOp",EDGE,"E14.20.2"),sQuery(id+"F0.wireOp",EDGE,"E14.20.3"),sQuery(id+"F0.wireOp",EDGE,"E14.20.4"),sQuery(id+"F0.wireOp",EDGE,"E14.20.5"),sQuery(id+"F0.wireOp",EDGE,"E14.20.6"),sQuery(id+"F0.wireOp",EDGE,"E14.20.7"),sQuery(id+"F0.wireOp",EDGE,"E14.20.8"),sQuery(id+"F0.wireOp",EDGE,"E14.20.9"),sQuery(id+"F0.wireOp",EDGE,"E14.21.0"),sQuery(id+"F0.wireOp",EDGE,"E14.21.1"),sQuery(id+"F0.wireOp",EDGE,"E14.21.2"),sQuery(id+"F0.wireOp",EDGE,"E14.21.3"),sQuery(id+"F0.wireOp",EDGE,"E14.21.4"),sQuery(id+"F0.wireOp",EDGE,"E14.21.5"),sQuery(id+"F0.wireOp",EDGE,"E14.21.6"),sQuery(id+"F0.wireOp",EDGE,"E14.21.7"),sQuery(id+"F0.wireOp",EDGE,"E14.21.8"),sQuery(id+"F0.wireOp",EDGE,"E14.21.9"),sQuery(id+"F0.wireOp",EDGE,"E14.22.0"),sQuery(id+"F0.wireOp",EDGE,"E14.22.1"),sQuery(id+"F0.wireOp",EDGE,"E14.22.2"),sQuery(id+"F0.wireOp",EDGE,"E14.22.3"),sQuery(id+"F0.wireOp",EDGE,"E14.22.4"),sQuery(id+"F0.wireOp",EDGE,"E14.22.5"),sQuery(id+"F0.wireOp",EDGE,"E14.22.6"),sQuery(id+"F0.wireOp",EDGE,"E14.22.7"),sQuery(id+"F0.wireOp",EDGE,"E14.22.8"),sQuery(id+"F0.wireOp",EDGE,"E14.22.9"),sQuery(id+"F0.wireOp",EDGE,"E14.23.0"),sQuery(id+"F0.wireOp",EDGE,"E14.23.1"),sQuery(id+"F0.wireOp",EDGE,"E14.23.2"),sQuery(id+"F0.wireOp",EDGE,"E14.23.3"),sQuery(id+"F0.wireOp",EDGE,"E14.23.4"),sQuery(id+"F0.wireOp",EDGE,"E14.23.5"),sQuery(id+"F0.wireOp",EDGE,"E14.23.6"),sQuery(id+"F0.wireOp",EDGE,"E14.23.7"),sQuery(id+"F0.wireOp",EDGE,"E14.23.8"),sQuery(id+"F0.wireOp",EDGE,"E14.23.9"),sQuery(id+"F0.wireOp",EDGE,"E14.24.0"),sQuery(id+"F0.wireOp",EDGE,"E14.24.1"),sQuery(id+"F0.wireOp",EDGE,"E14.24.2"),sQuery(id+"F0.wireOp",EDGE,"E14.24.3"),sQuery(id+"F0.wireOp",EDGE,"E14.24.4"),sQuery(id+"F0.wireOp",EDGE,"E14.24.5"),sQuery(id+"F0.wireOp",EDGE,"E14.24.6"),sQuery(id+"F0.wireOp",EDGE,"E14.24.7"),sQuery(id+"F0.wireOp",EDGE,"E14.24.8"),sQuery(id+"F0.wireOp",EDGE,"E14.24.9"),sQuery(id+"F0.wireOp",EDGE,"E14.25.0"),sQuery(id+"F0.wireOp",EDGE,"E14.25.1"),sQuery(id+"F0.wireOp",EDGE,"E14.25.2"),sQuery(id+"F0.wireOp",EDGE,"E14.25.3"),sQuery(id+"F0.wireOp",EDGE,"E14.25.4"),sQuery(id+"F0.wireOp",EDGE,"E14.25.5"),sQuery(id+"F0.wireOp",EDGE,"E14.25.6"),sQuery(id+"F0.wireOp",EDGE,"E14.25.7"),sQuery(id+"F0.wireOp",EDGE,"E14.25.8"),sQuery(id+"F0.wireOp",EDGE,"E14.25.9"),sQuery(id+"F0.wireOp",EDGE,"E14.26.0"),sQuery(id+"F0.wireOp",EDGE,"E14.26.1"),sQuery(id+"F0.wireOp",EDGE,"E14.26.2"),sQuery(id+"F0.wireOp",EDGE,"E14.26.3"),sQuery(id+"F0.wireOp",EDGE,"E14.26.4"),sQuery(id+"F0.wireOp",EDGE,"E14.26.5"),sQuery(id+"F0.wireOp",EDGE,"E14.26.6"),sQuery(id+"F0.wireOp",EDGE,"E14.26.7"),sQuery(id+"F0.wireOp",EDGE,"E14.26.8"),sQuery(id+"F0.wireOp",EDGE,"E14.26.9"),sQuery(id+"F0.wireOp",EDGE,"E14.27.0"),sQuery(id+"F0.wireOp",EDGE,"E14.27.1"),sQuery(id+"F0.wireOp",EDGE,"E14.27.2"),sQuery(id+"F0.wireOp",EDGE,"E14.27.3"),sQuery(id+"F0.wireOp",EDGE,"E14.27.4"),sQuery(id+"F0.wireOp",EDGE,"E14.27.5"),sQuery(id+"F0.wireOp",EDGE,"E14.27.6"),sQuery(id+"F0.wireOp",EDGE,"E14.27.7"),sQuery(id+"F0.wireOp",EDGE,"E14.27.8"),sQuery(id+"F0.wireOp",EDGE,"E14.27.9"),sQuery(id+"F0.wireOp",EDGE,"E14.28.0"),sQuery(id+"F0.wireOp",EDGE,"E14.28.1"),sQuery(id+"F0.wireOp",EDGE,"E14.28.2"),sQuery(id+"F0.wireOp",EDGE,"E14.28.3"),sQuery(id+"F0.wireOp",EDGE,"E14.28.4"),sQuery(id+"F0.wireOp",EDGE,"E14.28.5"),sQuery(id+"F0.wireOp",EDGE,"E14.28.6"),sQuery(id+"F0.wireOp",EDGE,"E14.28.7"),sQuery(id+"F0.wireOp",EDGE,"E14.28.8"),sQuery(id+"F0.wireOp",EDGE,"E14.28.9"),sQuery(id+"F0.wireOp",EDGE,"E14.29.0"),sQuery(id+"F0.wireOp",EDGE,"E14.29.1"),sQuery(id+"F0.wireOp",EDGE,"E14.29.2"),sQuery(id+"F0.wireOp",EDGE,"E14.29.3"),sQuery(id+"F0.wireOp",EDGE,"E14.29.4"),sQuery(id+"F0.wireOp",EDGE,"E14.29.5"),sQuery(id+"F0.wireOp",EDGE,"E14.29.6"),sQuery(id+"F0.wireOp",EDGE,"E14.29.7"),sQuery(id+"F0.wireOp",EDGE,"E14.29.8"),sQuery(id+"F0.wireOp",EDGE,"E14.29.9")])],"isStart":false})});
            extrude(context, id + "F4", {"entities" : qUnion([Q0]), "operationType" : NewBodyOperationType.REMOVE, "endBound" : BoundingType.THROUGH_ALL, "oppositeDirection" : true, "depth" : 25.4 * mm});
        }
    });
